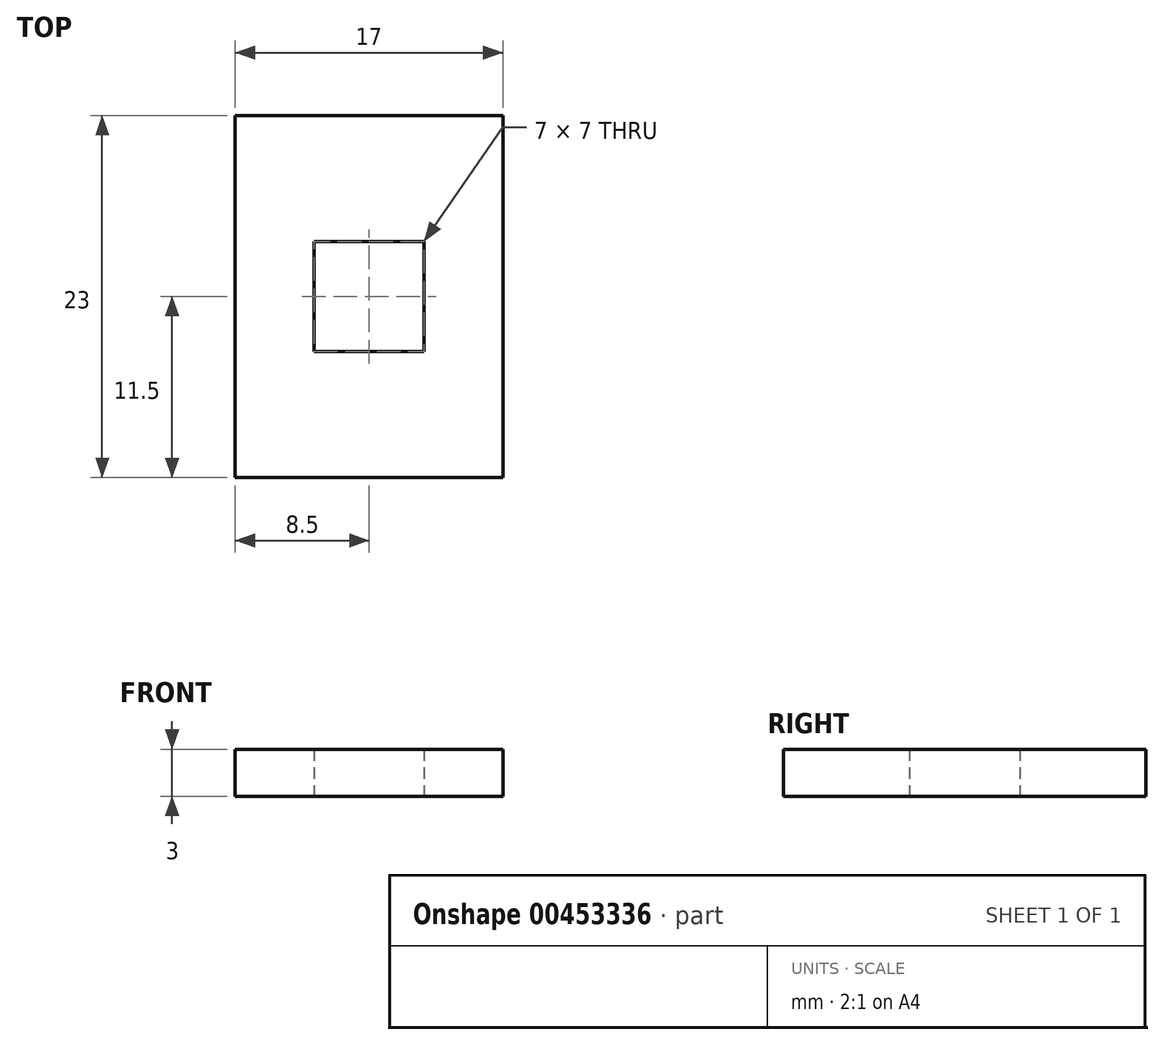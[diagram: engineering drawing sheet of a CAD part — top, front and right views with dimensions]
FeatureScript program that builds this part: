
annotation { "Feature Type Name" : "Feature", "Feature Type Description" : "" }
export const myFeature = defineFeature(function(context is Context, id is Id, definition is map)
    precondition{}
    {
        {
            var Q0;
            Q0=qCreatedBy(makeId("Top.planeOp"), FACE);
            var sketch = newSketch(context, id + "F0", { "sketchPlane" : qUnion([Q0])});
            skLineSegment(sketch, "E0.bottom", {"start": v(8.5, 11.5) * mm, "end": v(-8.5, 11.5) * mm});
            skLineSegment(sketch, "E0.top", {"start": v(8.5, -11.5) * mm, "end": v(-8.5, -11.5) * mm});
            skLineSegment(sketch, "E0.left", {"start": v(8.5, 11.5) * mm, "end": v(8.5, -11.5) * mm});
            skLineSegment(sketch, "E0.right", {"start": v(-8.5, 11.5) * mm, "end": v(-8.5, -11.5) * mm});
            skPoint(sketch, "E0.middle", {"position": v(0, 0) * mm});
            skLineSegment(sketch, "E1.bottom", {"start": v(3.5, 3.5) * mm, "end": v(-3.5, 3.5) * mm});
            skLineSegment(sketch, "E1.top", {"start": v(3.5, -3.5) * mm, "end": v(-3.5, -3.5) * mm});
            skLineSegment(sketch, "E1.left", {"start": v(3.5, 3.5) * mm, "end": v(3.5, -3.5) * mm});
            skLineSegment(sketch, "E1.right", {"start": v(-3.5, 3.5) * mm, "end": v(-3.5, -3.5) * mm});
            skSolve(sketch);
        }
        {
            var Q0;
            Q0 = qSketchRegion(id + "F0", true);
            extrude(context, id + "F1", {"entities" : qUnion([Q0]), "depth" : 3 * mm, "offsetDistance" : 25 * mm});
        }
    });
